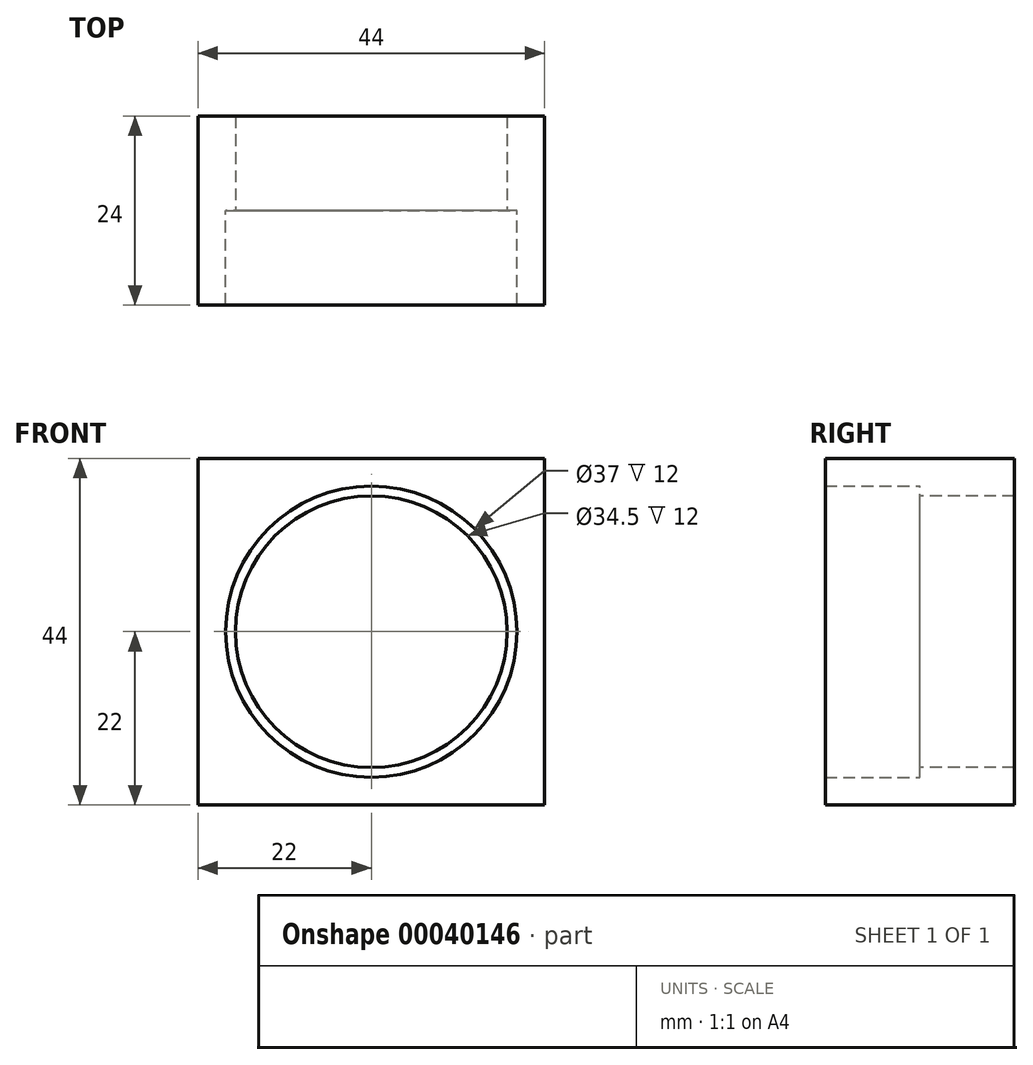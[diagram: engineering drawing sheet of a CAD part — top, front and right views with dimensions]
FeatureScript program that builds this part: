
annotation { "Feature Type Name" : "Feature", "Feature Type Description" : "" }
export const myFeature = defineFeature(function(context is Context, id is Id, definition is map)
    precondition{}
    {
        {
            var Q0;
            Q0=qCreatedBy(makeId("Front.planeOp"),FACE);
            var sketch = newSketch(context, id + "F0", { "sketchPlane" : qUnion([Q0])});
            skLineSegment(sketch, "E0.rect.bottom", {"start": v(22, 22) * mm, "end": v(-22, 22) * mm});
            skLineSegment(sketch, "E0.rect.top", {"start": v(22, -22) * mm, "end": v(-22, -22) * mm});
            skLineSegment(sketch, "E0.rect.left", {"start": v(22, 22) * mm, "end": v(22, -22) * mm});
            skLineSegment(sketch, "E0.rect.right", {"start": v(-22, 22) * mm, "end": v(-22, -22) * mm});
            skPoint(sketch, "E0.rect.middle", {"position": v(0, 0) * mm});
            skCircle(sketch, "E1", {"center": v(0, 0) * mm, "radius": 18.5 * mm});
            skSolve(sketch);
        }
        {
            var Q0;
            Q0 = qSketchRegion(id + "F0", true);
            var Q1;
            Q1 = qSketchRegion(id + "FMPEgLqjhURbu8I_1", true);
            extrude(context, id + "F1", {"entities" : qUnion([Q0, Q1]), "depth" : 12 * mm});
        }
        {
            var Q0;
            Q0=qCreatedBy(makeId("Front.planeOp"),FACE);
            var sketch = newSketch(context, id + "F2", { "sketchPlane" : qUnion([Q0])});
            skCircle(sketch, "E2", {"center": v(0, 0) * mm, "radius": 17.25 * mm});
            skLineSegment(sketch, "E3.rect.bottom", {"start": v(22, 22) * mm, "end": v(-22, 22) * mm});
            skLineSegment(sketch, "E3.rect.top", {"start": v(22, -22) * mm, "end": v(-22, -22) * mm});
            skLineSegment(sketch, "E3.rect.left", {"start": v(22, 22) * mm, "end": v(22, -22) * mm});
            skLineSegment(sketch, "E3.rect.right", {"start": v(-22, 22) * mm, "end": v(-22, -22) * mm});
            skSolve(sketch);
        }
        {
            var Q0;
            Q0=makeQuery(id+"F2.imprint","IMPRINT",FACE,{"disambiguationData":[TD([[makeQuery(id+"F2.imprint","IMPRINT",EDGE,{"derivedFrom":sQuery(id+"F2.wireOp",EDGE,"E2")}),-1.0]])]});
            extrude(context, id + "F3", {"entities" : qUnion([Q0]), "operationType" : NewBodyOperationType.ADD, "oppositeDirection" : true, "depth" : 12 * mm});
        }
    });
